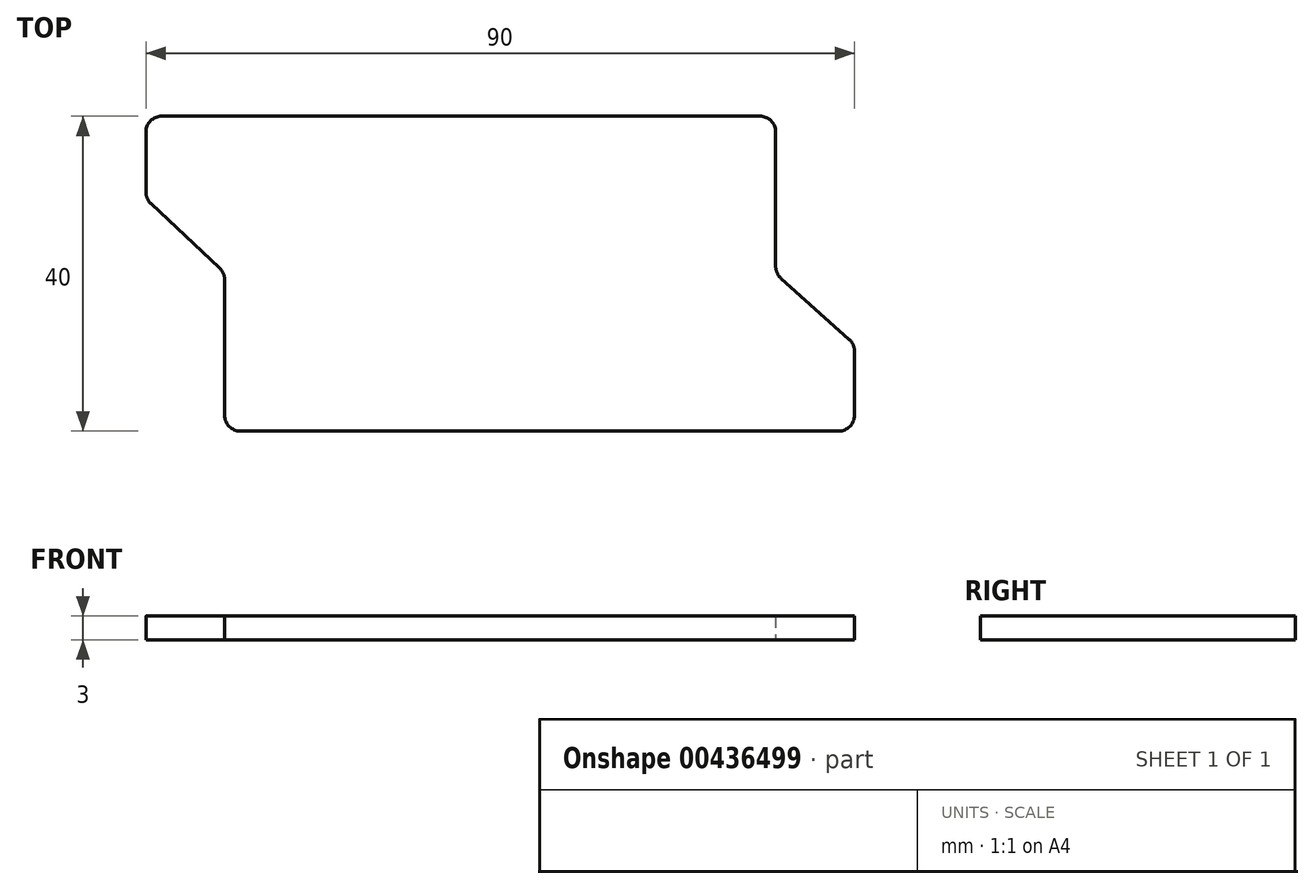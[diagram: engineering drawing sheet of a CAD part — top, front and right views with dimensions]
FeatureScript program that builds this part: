
annotation { "Feature Type Name" : "Feature", "Feature Type Description" : "" }
export const myFeature = defineFeature(function(context is Context, id is Id, definition is map)
    precondition{}
    {
        {
            var Q0;
            Q0=qCreatedBy(makeId("Top.planeOp"),FACE);
            var sketch = newSketch(context, id + "F0", { "sketchPlane" : qUnion([Q0])});
            skLineSegment(sketch, "E0.bottom", {"start": v(-18.15, 7.15) * mm, "end": v(61.85, 7.15) * mm});
            skLineSegment(sketch, "E0.top", {"start": v(-8.15, -32.85) * mm, "end": v(71.85, -32.85) * mm});
            skLineSegment(sketch, "E0.left", {"start": v(-18.15, 7.15) * mm, "end": v(-18.15, -3.36) * mm});
            skLineSegment(sketch, "E0.right", {"start": v(71.85, -21.8) * mm, "end": v(71.85, -32.85) * mm});
            skLineSegment(sketch, "E1.0", {"start": v(-8.15, 7.4) * mm, "end": v(-8.15, -32.85) * mm});
            skLineSegment(sketch, "E2.0", {"start": v(61.85, 7.15) * mm, "end": v(61.85, -32.85) * mm});
            skLineSegment(sketch, "E3", {"start": v(-18.15, -3.36) * mm, "end": v(-8.15, -12.73) * mm});
            skLineSegment(sketch, "E4", {"start": v(71.85, -21.8) * mm, "end": v(61.85, -12.85) * mm});
            skSolve(sketch);
        }
        {
            var Q0;
            Q0 = qSketchRegion(id + "F0", true);
            extrude(context, id + "F1", {"entities" : qUnion([Q0]), "depth" : 3 * mm});
        }
        {
            var Q0;
            Q0=makeQuery(id+"F1.opExtrude","SWEPT_EDGE",EDGE,{"disambiguationData":[OSD([sQuery(id+"F0.wireOp",EDGE,"E0.bottom"),sQuery(id+"F0.wireOp",EDGE,"E0.left")])]});
            var Q1;
            Q1=makeQuery(id+"F1.opExtrude","SWEPT_EDGE",EDGE,{"disambiguationData":[OSD([sQuery(id+"F0.wireOp",EDGE,"E0.left"),sQuery(id+"F0.wireOp",EDGE,"E3")])]});
            var Q2;
            Q2=makeQuery(id+"F1.opExtrude","SWEPT_EDGE",EDGE,{"disambiguationData":[OSD([sQuery(id+"F0.wireOp",EDGE,"E1.0"),sQuery(id+"F0.wireOp",EDGE,"E3")])]});
            var Q3;
            Q3=makeQuery(id+"F1.opExtrude","SWEPT_EDGE",EDGE,{"disambiguationData":[OSD([sQuery(id+"F0.wireOp",EDGE,"E0.top"),sQuery(id+"F0.wireOp",EDGE,"E1.0")])]});
            var Q4;
            Q4=makeQuery(id+"F1.opExtrude","SWEPT_EDGE",EDGE,{"disambiguationData":[OSD([sQuery(id+"F0.wireOp",EDGE,"E0.top"),sQuery(id+"F0.wireOp",EDGE,"E0.right")])]});
            var Q5;
            Q5=makeQuery(id+"F1.opExtrude","SWEPT_EDGE",EDGE,{"disambiguationData":[OSD([sQuery(id+"F0.wireOp",EDGE,"E0.right"),sQuery(id+"F0.wireOp",EDGE,"E4")])]});
            var Q6;
            Q6=makeQuery(id+"F1.opExtrude","SWEPT_EDGE",EDGE,{"disambiguationData":[OSD([sQuery(id+"F0.wireOp",EDGE,"E2.0"),sQuery(id+"F0.wireOp",EDGE,"E4")])]});
            var Q7;
            Q7=makeQuery(id+"F1.opExtrude","SWEPT_EDGE",EDGE,{"disambiguationData":[OSD([sQuery(id+"F0.wireOp",EDGE,"E0.bottom"),sQuery(id+"F0.wireOp",EDGE,"E2.0")])]});
            fillet(context, id + "F2", {"entities" : qUnion([Q0, Q1, Q2, Q3, Q4, Q5, Q6, Q7]), "radius" : 2 * mm, "tangentPropagation" : true, "allowEdgeOverflow" : false});
        }
    });
